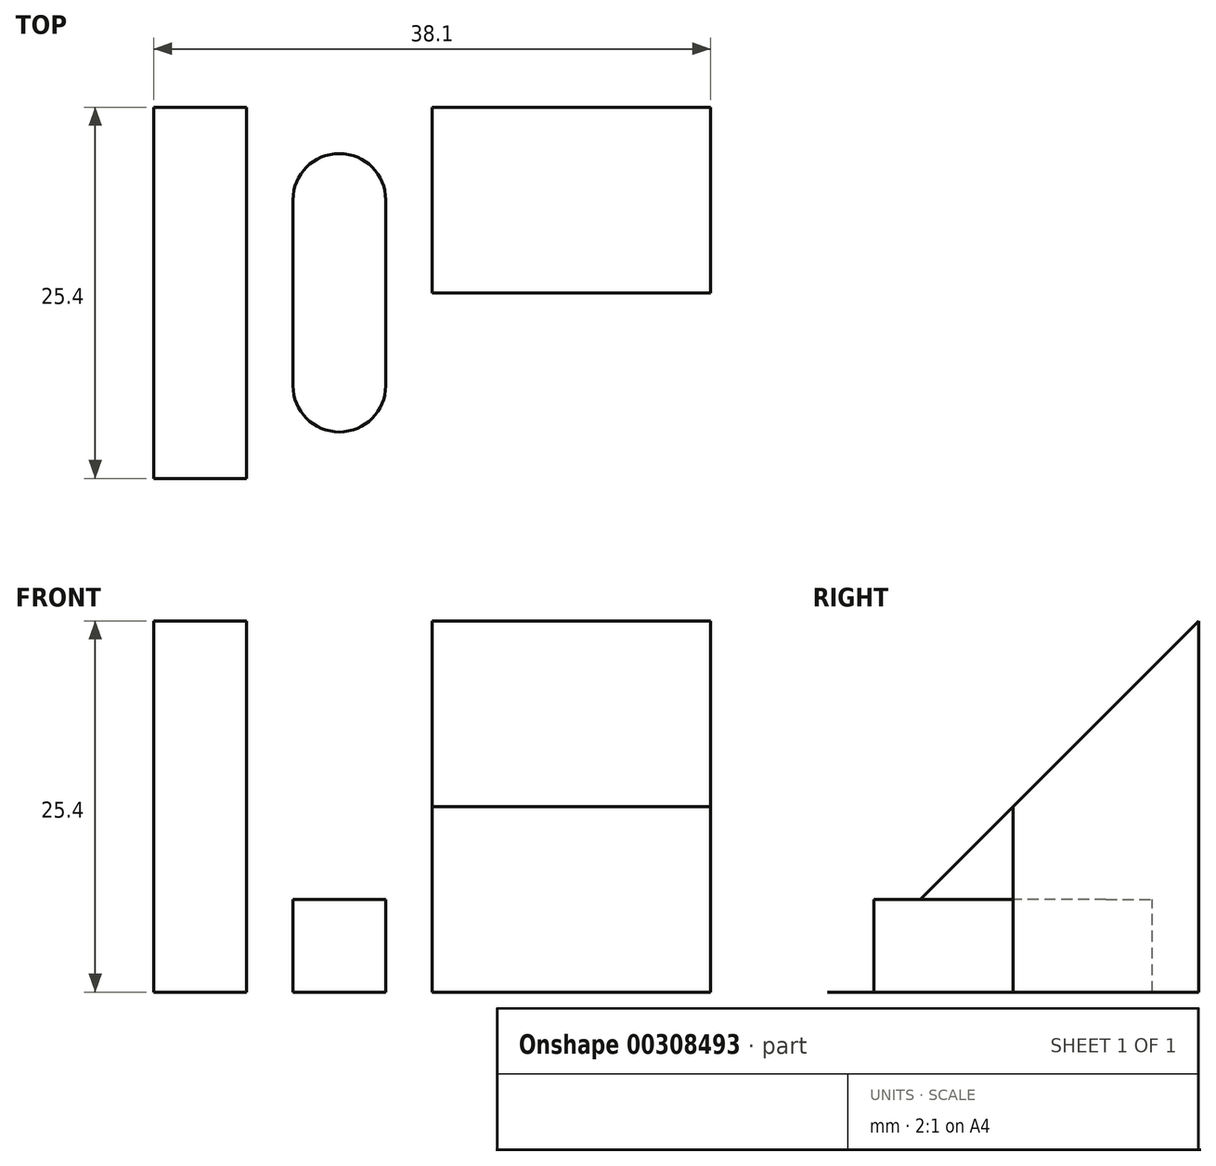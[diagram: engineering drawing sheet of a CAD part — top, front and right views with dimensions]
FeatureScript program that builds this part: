
annotation { "Feature Type Name" : "Feature", "Feature Type Description" : "" }
export const myFeature = defineFeature(function(context is Context, id is Id, definition is map)
    precondition{}
    {
        {
            var Q0;
            Q0=qCreatedBy(makeId("Front.planeOp"),FACE);
            var sketch = newSketch(context, id + "F0", { "sketchPlane" : qUnion([Q0])});
            skLineSegment(sketch, "E0.bottom", {"start": v(0, 0) * mm, "end": v(38.1, 0) * mm});
            skLineSegment(sketch, "E0.top", {"start": v(0, 25.4) * mm, "end": v(38.1, 25.4) * mm});
            skLineSegment(sketch, "E0.left", {"start": v(0, 0) * mm, "end": v(0, 25.4) * mm});
            skLineSegment(sketch, "E0.right", {"start": v(38.1, 0) * mm, "end": v(38.1, 25.4) * mm});
            skSolve(sketch);
        }
        {
            var Q0;
            Q0 = qSketchRegion(id + "F0", true);
            extrude(context, id + "F1", {"entities" : qUnion([Q0]), "oppositeDirection" : true, "depth" : 25.4 * mm});
        }
        {
            var Q0;
            Q0=makeQuery(id+"F1.opExtrude","SWEPT_FACE",FACE,{"disambiguationData":[OSD([sQuery(id+"F0.wireOp",EDGE,"E0.right")])]});
            var sketch = newSketch(context, id + "F2", { "sketchPlane" : qUnion([Q0])});
            skLineSegment(sketch, "E1", {"start": v(12.7, 25.4) * mm, "end": v(12.7, 0) * mm});
            skLineSegment(sketch, "E2", {"start": v(25.4, 25.4) * mm, "end": v(12.7, 12.7) * mm});
            skLineSegment(sketch, "E3", {"start": v(12.7, 6.35) * mm, "end": v(0, 6.35) * mm});
            skSolve(sketch);
        }
        {
            var Q0;
            {var subQ4=sQuery(id+"F2.wireOp",EDGE,"E2");Q0=makeQuery(id+"F2.imprint","IMPRINT",FACE,{"disambiguationData":[TD([[makeQuery(id+"F2.imprint","IMPRINT",EDGE,{"derivedFrom":subQ4}),-1.0]])]});}
            extrude(context, id + "F3", {"entities" : qUnion([Q0]), "operationType" : NewBodyOperationType.REMOVE, "oppositeDirection" : true, "depth" : 50.8 * mm});
        }
        {
            var Q0;
            {var subQ6=sQuery(id+"F2.wireOp",EDGE,"E3");Q0=makeQuery(id+"F2.imprint","IMPRINT",FACE,{"disambiguationData":[TD([[makeQuery(id+"F2.imprint","IMPRINT",EDGE,{"derivedFrom":subQ6}),-1.0]])]});}
            extrude(context, id + "F4", {"entities" : qUnion([Q0]), "operationType" : NewBodyOperationType.REMOVE, "oppositeDirection" : true, "depth" : 19.05 * mm});
        }
        {
            var Q0;
            Q0=makeQuery(id+"F1.opExtrude","CAP_FACE",FACE,{"disambiguationData":[OSD([sQuery(id+"F0.wireOp",EDGE,"E0.bottom"),sQuery(id+"F0.wireOp",EDGE,"E0.top"),sQuery(id+"F0.wireOp",EDGE,"E0.left"),sQuery(id+"F0.wireOp",EDGE,"E0.right")])],"isStart":true});
            var sketch = newSketch(context, id + "F5", { "sketchPlane" : qUnion([Q0])});
            skLineSegment(sketch, "E4", {"start": v(19.05, 6.35) * mm, "end": v(6.35, 6.35) * mm});
            skLineSegment(sketch, "E5", {"start": v(6.35, 6.35) * mm, "end": v(6.35, 0) * mm});
            skLineSegment(sketch, "E6", {"start": v(6.35, 6.35) * mm, "end": v(6.35, 25.4) * mm});
            skSolve(sketch);
        }
        {
            var Q0;
            Q0=makeQuery(id+"F5.imprint","IMPRINT",FACE,{"disambiguationData":[TD([[makeQuery(id+"F5.imprint","IMPRINT",EDGE,{"derivedFrom":sQuery(id+"F5.wireOp",EDGE,"E4")}),-1.0]])]});
            extrude(context, id + "F6", {"entities" : qUnion([Q0]), "operationType" : NewBodyOperationType.REMOVE, "oppositeDirection" : true, "depth" : 25.4 * mm});
        }
        {
            var Q0;
            Q0=makeQuery(id+"F1.opExtrude","SWEPT_FACE",FACE,{"disambiguationData":[OSD([sQuery(id+"F0.wireOp",EDGE,"E0.left")])]});
            var sketch = newSketch(context, id + "F7", { "sketchPlane" : qUnion([Q0])});
            skLineSegment(sketch, "E7", {"start": v(-12.7, 12.7) * mm, "end": v(0, 0) * mm});
            skSolve(sketch);
        }
        {
            var Q0;
            Q0=makeQuery(id+"F7.imprint","IMPRINT",FACE,{"disambiguationData":[TD([[makeQuery(id+"F7.imprint","IMPRINT",EDGE,{"derivedFrom":sQuery(id+"F7.wireOp",EDGE,"E7")}),1.0]])]});
            extrude(context, id + "F8", {"entities" : qUnion([Q0]), "operationType" : NewBodyOperationType.REMOVE, "oppositeDirection" : true, "depth" : 6.35 * mm});
        }
        {
            var Q0;
            {var subQ4=sQuery(id+"F2.wireOp",EDGE,"E3");Q0=makeQuery(id+"F2.imprint","IMPRINT",FACE,{"disambiguationData":[TD([[makeQuery(id+"F2.imprint","IMPRINT",EDGE,{"derivedFrom":subQ4}),1.0]])]});}
            extrude(context, id + "F9", {"entities" : qUnion([Q0]), "operationType" : NewBodyOperationType.REMOVE, "oppositeDirection" : true, "depth" : 19.05 * mm});
        }
        {
            var Q0;
            Q0=makeQuery(id+"F6.boolean.opBoolean","MERGE",FACE,{"derivedFrom":[makeQuery(id+"F4.boolean.opBoolean","COPY",FACE,{"derivedFrom":makeQuery(id+"F4.opExtrude","SWEPT_FACE",FACE,{"disambiguationData":[OSD([sQuery(id+"F2.wireOp",EDGE,"E3")])]})}),makeQuery(id+"F6.opExtrude","SWEPT_FACE",FACE,{"disambiguationData":[OSD([sQuery(id+"F5.wireOp",EDGE,"E4")])]})]});
            var sketch = newSketch(context, id + "F10", { "sketchPlane" : qUnion([Q0])});
            skLineSegment(sketch, "E8", {"start": v(12.7, 19.05) * mm, "end": v(12.7, 6.35) * mm, "construction": true});
            skArc(sketch, "E9.0.startCap", {"start": v(9.53, 19.05) * mm, "mid": v(12.7, 22.23) * mm, "end": v(15.88, 19.05) * mm});
            skArc(sketch, "E9.0.endCap", {"start": v(15.88, 6.35) * mm, "mid": v(12.7, 3.18) * mm, "end": v(9.53, 6.35) * mm});
            skLineSegment(sketch, "E9.0.left", {"start": v(15.88, 19.05) * mm, "end": v(15.88, 6.35) * mm});
            skLineSegment(sketch, "E9.0.right", {"start": v(9.53, 19.05) * mm, "end": v(9.53, 6.35) * mm});
            skSolve(sketch);
        }
        {
            var Q0;
            Q0=makeQuery(id+"F10.imprint","IMPRINT",FACE,{"disambiguationData":[TD([[makeQuery(id+"F10.imprint","IMPRINT",EDGE,{"derivedFrom":sQuery(id+"F10.wireOp",EDGE,"E9.0.startCap")}),-1.0]])]});
            extrude(context, id + "F11", {"entities" : qUnion([Q0]), "operationType" : NewBodyOperationType.REMOVE, "oppositeDirection" : true, "depth" : 25.4 * mm});
        }
    });
